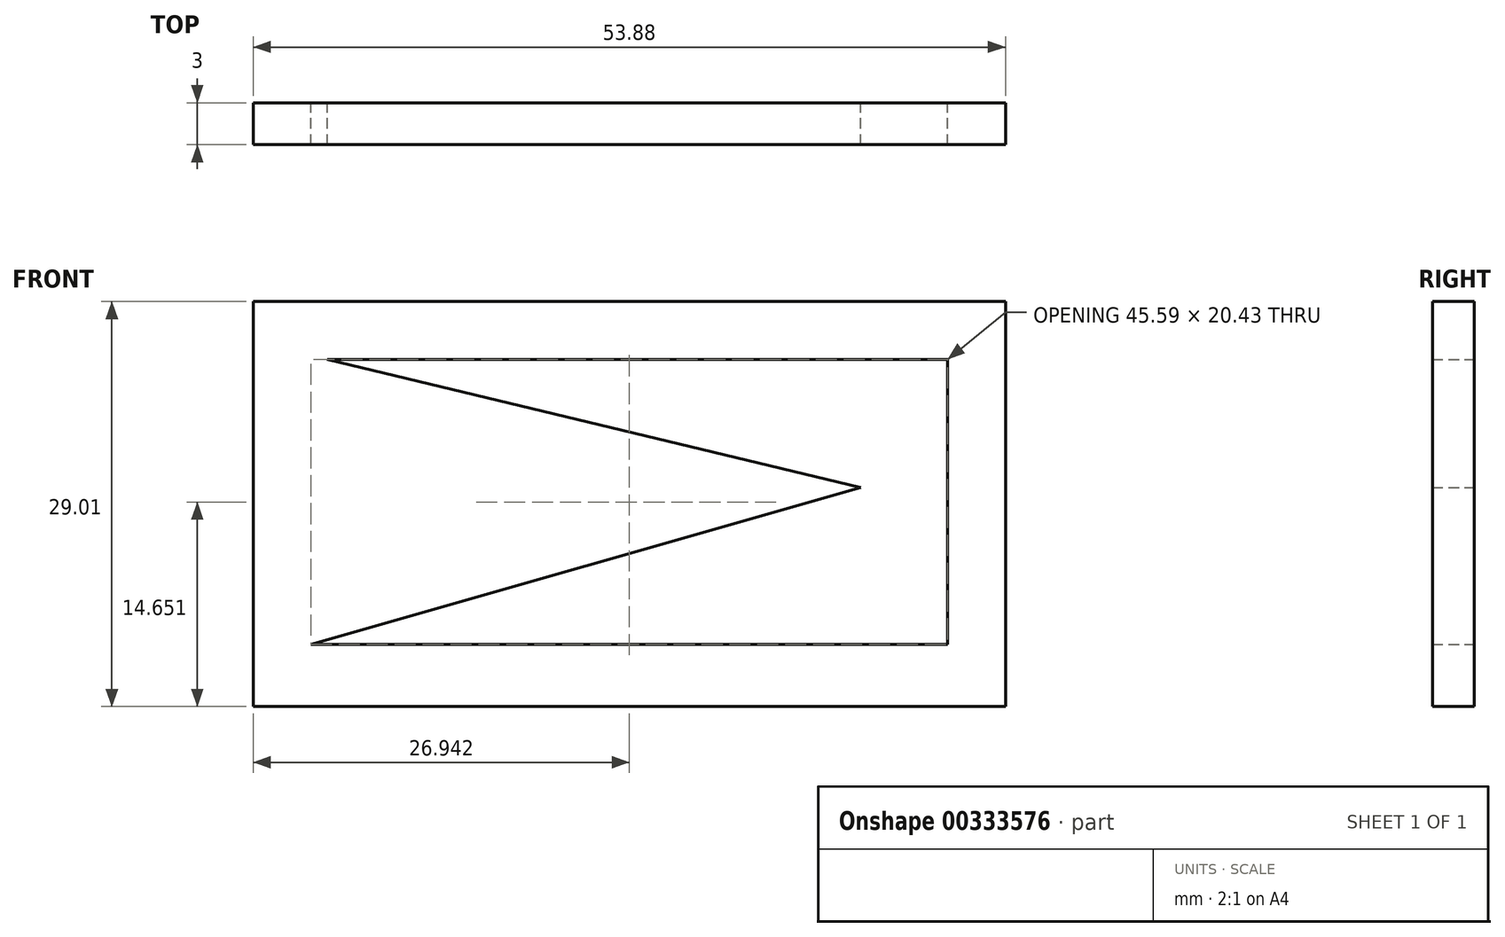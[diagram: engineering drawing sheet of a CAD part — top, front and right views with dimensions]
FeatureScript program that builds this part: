
annotation { "Feature Type Name" : "Feature", "Feature Type Description" : "" }
export const myFeature = defineFeature(function(context is Context, id is Id, definition is map)
    precondition{}
    {
        {
            var Q0;
            Q0=qCreatedBy(makeId("Front.planeOp"),FACE);
            var sketch = newSketch(context, id + "F0", { "sketchPlane" : qUnion([Q0])});
            skLineSegment(sketch, "E0", {"start": v(-6.22, -14.21) * mm, "end": v(-60.1, -14.21) * mm});
            skLineSegment(sketch, "E1", {"start": v(-60.1, -14.21) * mm, "end": v(-60.1, -43.22) * mm});
            skLineSegment(sketch, "E2", {"start": v(-60.1, -43.22) * mm, "end": v(-6.22, -43.22) * mm});
            skLineSegment(sketch, "E3", {"start": v(-6.22, -43.22) * mm, "end": v(-6.22, -14.21) * mm});
            skLineSegment(sketch, "E4", {"start": v(-10.36, -18.36) * mm, "end": v(-54.77, -18.36) * mm});
            skLineSegment(sketch, "E5", {"start": v(-54.77, -18.36) * mm, "end": v(-16.58, -27.53) * mm});
            skLineSegment(sketch, "E6", {"start": v(-16.58, -27.53) * mm, "end": v(-55.95, -38.78) * mm});
            skLineSegment(sketch, "E7", {"start": v(-55.95, -38.78) * mm, "end": v(-10.36, -38.78) * mm});
            skLineSegment(sketch, "E8", {"start": v(-10.36, -38.78) * mm, "end": v(-10.36, -18.36) * mm});
            skSolve(sketch);
        }
        {
            var Q0;
            Q0=makeQuery(id+"F0.imprint","IMPRINT",FACE,{"disambiguationData":[TD([[makeQuery(id+"F0.imprint","IMPRINT",EDGE,{"derivedFrom":sQuery(id+"F0.wireOp",EDGE,"E0")}),1.0]])]});
            extrude(context, id + "F1", {"entities" : qUnion([Q0]), "depth" : 3 * mm});
        }
    });
